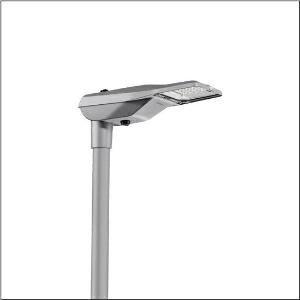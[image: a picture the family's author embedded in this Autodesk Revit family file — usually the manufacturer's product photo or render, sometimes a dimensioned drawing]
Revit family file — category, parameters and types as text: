
# Revit family: streetlight_sl_21_iq_micro___st1_0ab_5xe1m31y08cb_a08b
name_source: partatom
category: Lighting Fixtures
units: mm (PartAtom-declared; Revit-internal decimal feet)

## family parameters
Cut with Voids When Loaded = No
Host = Face
Light Source = No
Part Type = Normal
Room Calculation Point = No
Round Connector Dimension = Use Diameter
Shared = No

## types (1)
- --- (1 x LED, 2530 lm, 19.1 W, 3000K)
    Apparent Load = 19 VA
    CIE Flux Codes = 38 73 97 100 100
    Color Rendering = 70
    Color Temperature = 3000K
    Default Elevation = 1800 mm
    Description = Streetlight SL 21 iQ micro, mast luminaire, primary light control with lens, of PMMA, primary optical cover: cover, of toughened safety glass, transparent, light distribution: ST1.0aB, light emission: direct distribution, primary light characteristic: asymmetric, installation type: post-top, side-entry, LED, High Power LED, rated luminous flux: 2.530lm, luminous efficacy: 133lm/W, light colour: 730, colour temperature: 3000K, control: presetting dimming logarithmic, Street-Remote, Auto-Match, Temp-Guard, Lumen-Switch, Night-Set, Smart-Wire, Light-Fading, Desk-Remote (wireless, voltage-free reading and setting of iQ features in the workshop via application-optimized NFC function/RFID function), optimised constant luminous flux control (CLO 2.0), mains connection: 220..240V, AC, 50/60Hz, start of lifetime: 19W, end of service life: 20W, reduction: 9W, luminaire housing, of diecast aluminium, powder-coated, Siteco® metallic grey (DB 702S), corrosivity category C5 mid according to DIN EN ISO 12944, please order mast flange separately, inclination adjustable: 0°, 5°, 10°, 15°, sealing non-destructively replaceable, multi-level sealing system, length: 528mm, width: 235mm, height: 110mm, mast flange for spigot size: 42mm (side-entry): 5XC10008XM4, 60/48mm (side-entry/post-top): 5XC10108XM2, 76/60mm (side-entry/post-top): 5XC10108XM1, Smart Interface below and above, protection rating (complete): IP66, insulation class (complete): insulation class II (safety insulation), certification: CE, ENEC, ENEC+, VDE, impact resistance: IK09, permissible operating ambient temperature for outdoor applications: -40..+50°C, standard-compliant lighting for roads and squares, packaging unit: 1 piece

Light Distribution: ST1.0aB
    Height = 110 mm
    Lamp = 1 x LED
    Lamp Light Flux = 2530 lm
    Lamp Power = 19.1 W
    Lamp count = 1
    Length = 528 mm
    Luminous efficacy = 132 lm/W
    Manufacturer = Siteco
    ModVariant = No
    Model = 5XE1M31Y08CB
    Number of Poles = 1
    OnlyDefault = Yes
    Power Factor = 1
    Product Name = Streetlight SL 21 iQ micro | ST1.0aB
    Product group = mast luminaire | pylon top
    ProductGroupID = 6100
    Protection Class = Protection class II
    Protection Degree = IP 66
    RLX_Detail_Level = 1
    RLX_Emergency_Light_Flux = 0 lm
    RLX_Emergency_Type = 0
    RLX_Emergency_Type_DB = No
    RlxData = <blob elided: 98749 chars, md5=fd84282f>
    Socket = socket
    Standby Power = 0 W
    System Light Flux = 2530 lm
    System Power = 19 W
    Type Comments = factory setting: luminous flux: 100 % | dim-lin: 254 | 387 mA
    Type Image = l_1007239.jpg
    URL = http://relux.com
    VarID = @adj_042755
    Voltage = 0 V
    Weight = 0.00 kg
    Width = 235 mm

## geometry (parser evidence)
native form markers: Blend x4, Sweep x10
no freeform markers — native parametric forms only
